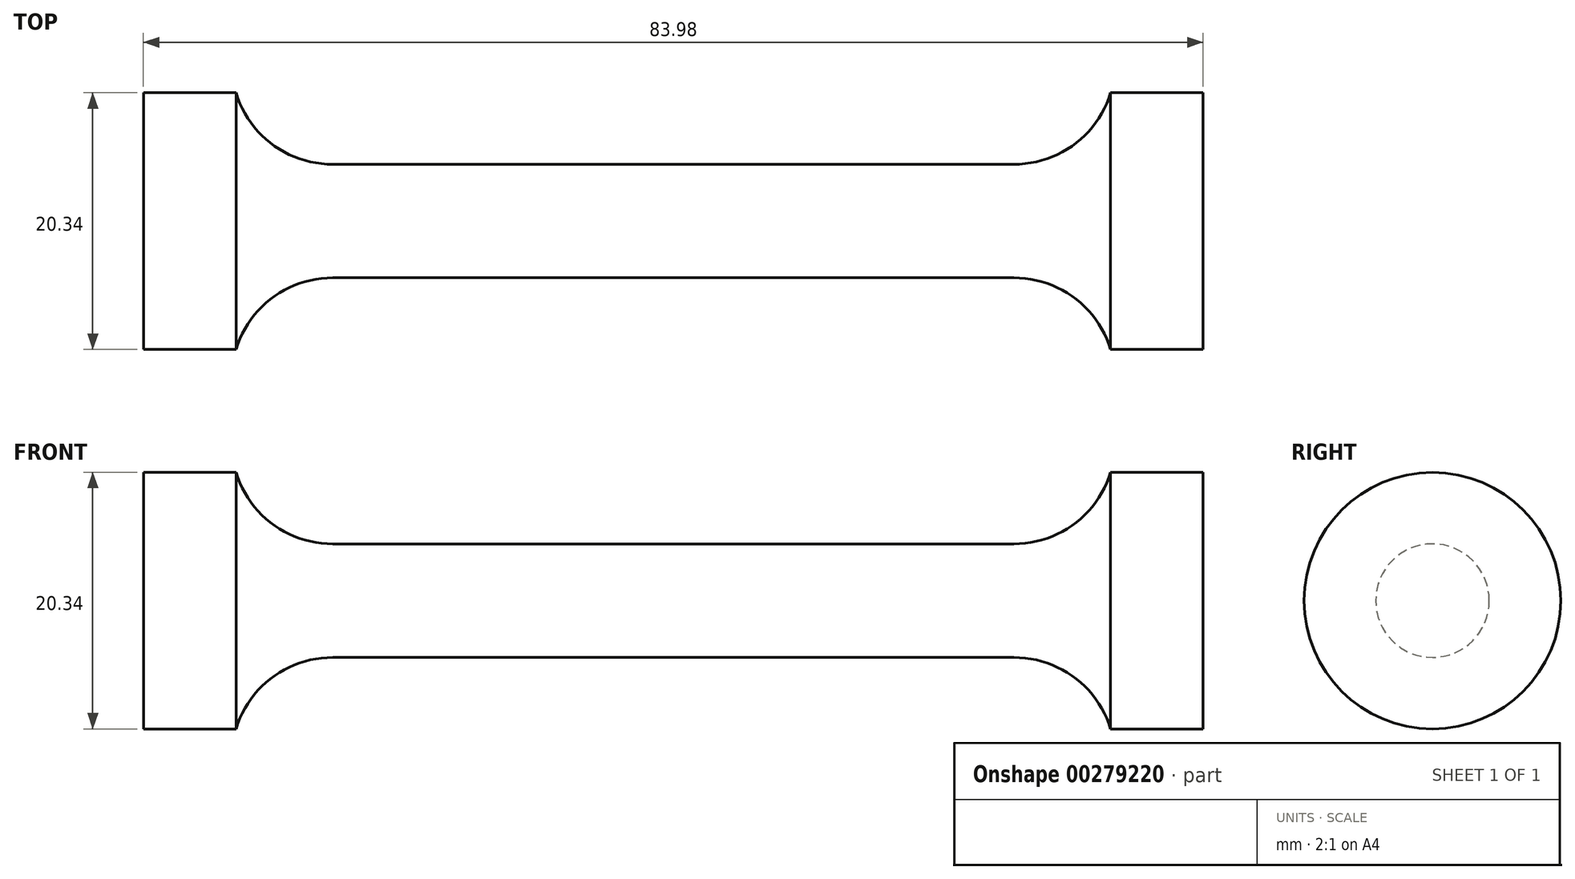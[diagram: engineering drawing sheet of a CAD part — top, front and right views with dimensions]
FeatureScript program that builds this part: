
annotation { "Feature Type Name" : "Feature", "Feature Type Description" : "" }
export const myFeature = defineFeature(function(context is Context, id is Id, definition is map)
    precondition{}
    {
        {
            var Q0;
            Q0=qCreatedBy(makeId("Front.planeOp"),FACE);
            var sketch = newSketch(context, id + "F0", { "sketchPlane" : qUnion([Q0])});
            skLineSegment(sketch, "E0", {"start": v(0, 4.5) * mm, "end": v(27, 4.5) * mm});
            skArc(sketch, "E1", {"start": v(27, 4.5) * mm, "mid": v(31.76, 6.07) * mm, "end": v(34.65, 10.17) * mm});
            skLineSegment(sketch, "E2", {"start": v(34.65, 10.17) * mm, "end": v(41.99, 10.17) * mm});
            skLineSegment(sketch, "E3", {"start": v(41.99, 10.17) * mm, "end": v(41.99, 0) * mm});
            skLineSegment(sketch, "E4.MirrorCS", {"start": v(0, 4.5) * mm, "end": v(-27, 4.5) * mm});
            skLineSegment(sketch, "E5.MirrorCS", {"start": v(-41.99, 10.17) * mm, "end": v(-41.99, 0) * mm});
            skLineSegment(sketch, "E6.MirrorCS", {"start": v(-34.65, 10.17) * mm, "end": v(-41.99, 10.17) * mm});
            skArc(sketch, "E7.MirrorCS", {"start": v(-27, 4.5) * mm, "mid": v(-31.76, 6.07) * mm, "end": v(-34.65, 10.17) * mm});
            skLineSegment(sketch, "E8", {"start": v(-41.99, 0) * mm, "end": v(41.99, 0) * mm});
            skSolve(sketch);
        }
        {
            var Q0;
            Q0 = qSketchRegion(id + "F0", true);
            var Q1;
            Q1=sQuery(id+"F0.wireOp",EDGE,"E8");
            revolve(context, id + "F1", {"entities" : qUnion([Q0]), "axis" : qUnion([Q1]), "revolveType" : RevolveType.FULL, "oppositeDirection" : true});
        }
    });
